FCSTD DOCUMENT  (FreeCAD 1.1R20260325 (Git shallow))
Label: Ruler
License: Creative Commons Attribution 4.0
LicenseURL: https://creativecommons.org/licenses/by/4.0/
objects: App::Point×1, Sketcher::SketchObject×1, PartDesign::Body×1
note: 3 computed .brp shape members not serialized (recipe doc carries the construction recipe); baked Part::Feature solids carry a one-line shape summary decoded from their .brp

FEATURE [App::Point] Origin001
  Role = Origin
FEATURE [Sketcher::SketchObject] Sketch
  ArcFitTolerance = 1e-06
  AttachmentSupport = -> [Origin]
  ExternalTypes = [0]
  FullyConstrained = false
  MakeInternals = true
  MapMode = 5
  Placement = pos=(0,0,0) rot=(1,0,0;1.5708rad)
  _ExternalGeoVersion = 1
  sketch-geometry (9):
    g0: LineSegment StartX=-113.465 StartY=45 StartZ=0 EndX=-113.465 EndY=0 EndZ=0
    g1: LineSegment StartX=-113.465 StartY=0 StartZ=0 EndX=113.465 EndY=0 EndZ=0
    g2: LineSegment StartX=113.465 StartY=0 StartZ=0 EndX=113.465 EndY=45 EndZ=0
    g3: LineSegment StartX=113.465 StartY=45 StartZ=0 EndX=-113.465 EndY=45 EndZ=0
    g4: Circle CenterX=-106.465 CenterY=38 CenterZ=0 NormalX=0 NormalY=0 NormalZ=1 AngleXU=0 Radius=2.5
    g5: LineSegment [constr] StartX=-106.465 StartY=38 StartZ=0 EndX=-106.465 EndY=45 EndZ=0
    g6: LineSegment [constr] StartX=-106.465 StartY=38 StartZ=0 EndX=-113.465 EndY=38 EndZ=0
    g7: Circle CenterX=-97.2029 CenterY=37.4103 CenterZ=0 NormalX=0 NormalY=0 NormalZ=1 AngleXU=0 Radius=1.5
    g8: Circle CenterX=-84.9623 CenterY=37.4103 CenterZ=0 NormalX=0 NormalY=0 NormalZ=1 AngleXU=0 Radius=1.5
  constraints (22):
    c: Coincident(g0,g1)
    c: Coincident(g1,g2)
    c: Coincident(g2,g3)
    c: Coincident(g3,g0)
    c: Vertical(g0)
    c: Vertical(g2)
    c: Horizontal(g1)
    c: PointOnObject(g1,g-1)
    c: Symmetric(g0,g2,g-2)
    c: Distance(g0,g0) = 45
    c: Diameter(g4) = 5
    c: Coincident(g5,g4)
    c: PointOnObject(g5,g3)
    c: Vertical(g5)
    c: Coincident(g6,g4)
    c: PointOnObject(g6,g0)
    c: Horizontal(g6)
    c: Equal(g6,g5)
    c: Distance(g5,g5) = 7
    c: Equal(g7,g8)
    c: Diameter(g8) = 3
    c: Horizontal(g7,g8)
FEATURE [PartDesign::Body] Body
  AllowCompound = false
  Group = -> [Sketch]
  Origin = -> Origin
